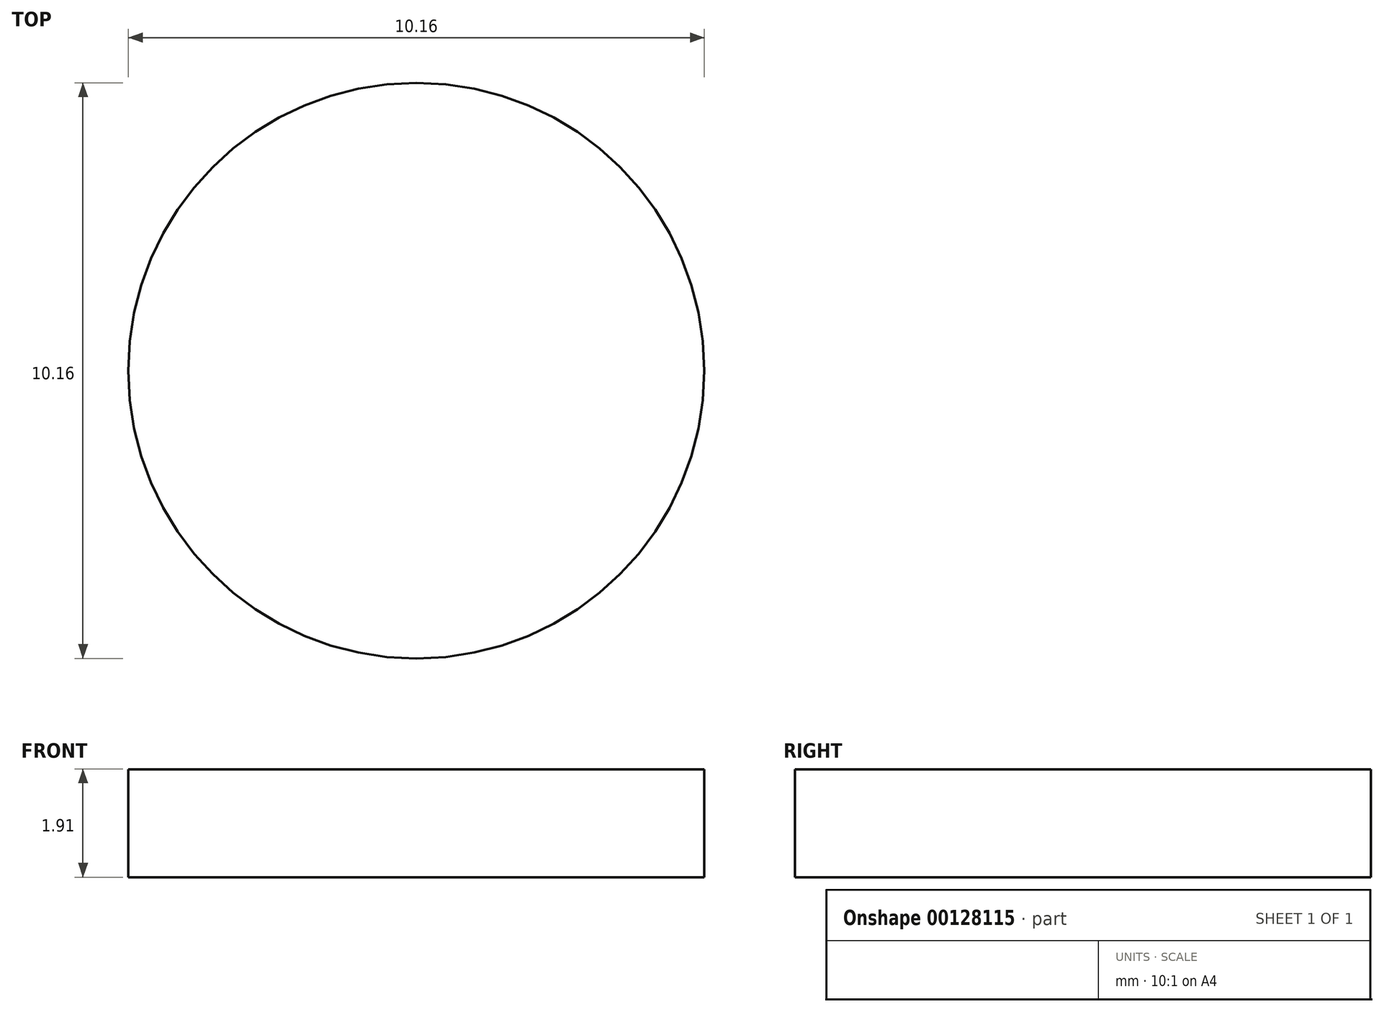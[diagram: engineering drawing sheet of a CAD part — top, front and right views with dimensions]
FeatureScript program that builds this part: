
annotation { "Feature Type Name" : "Feature", "Feature Type Description" : "" }
export const myFeature = defineFeature(function(context is Context, id is Id, definition is map)
    precondition{}
    {
        {
            var Q0;
            Q0=qCreatedBy(makeId("Top.planeOp"),FACE);
            var sketch = newSketch(context, id + "F0", { "sketchPlane" : qUnion([Q0])});
            skCircle(sketch, "E0", {"center": v(0, 0) * mm, "radius": 5.08 * mm});
            skSolve(sketch);
        }
        {
            var Q0;
            Q0=makeQuery(id+"F0.imprint","IMPRINT",FACE,{"disambiguationData":[TD([[makeQuery(id+"F0.imprint","IMPRINT",EDGE,{"derivedFrom":sQuery(id+"F0.wireOp",EDGE,"E0")}),1.0]])]});
            extrude(context, id + "F1", {"entities" : qUnion([Q0]), "depth" : 1.9 * mm});
        }
    });
